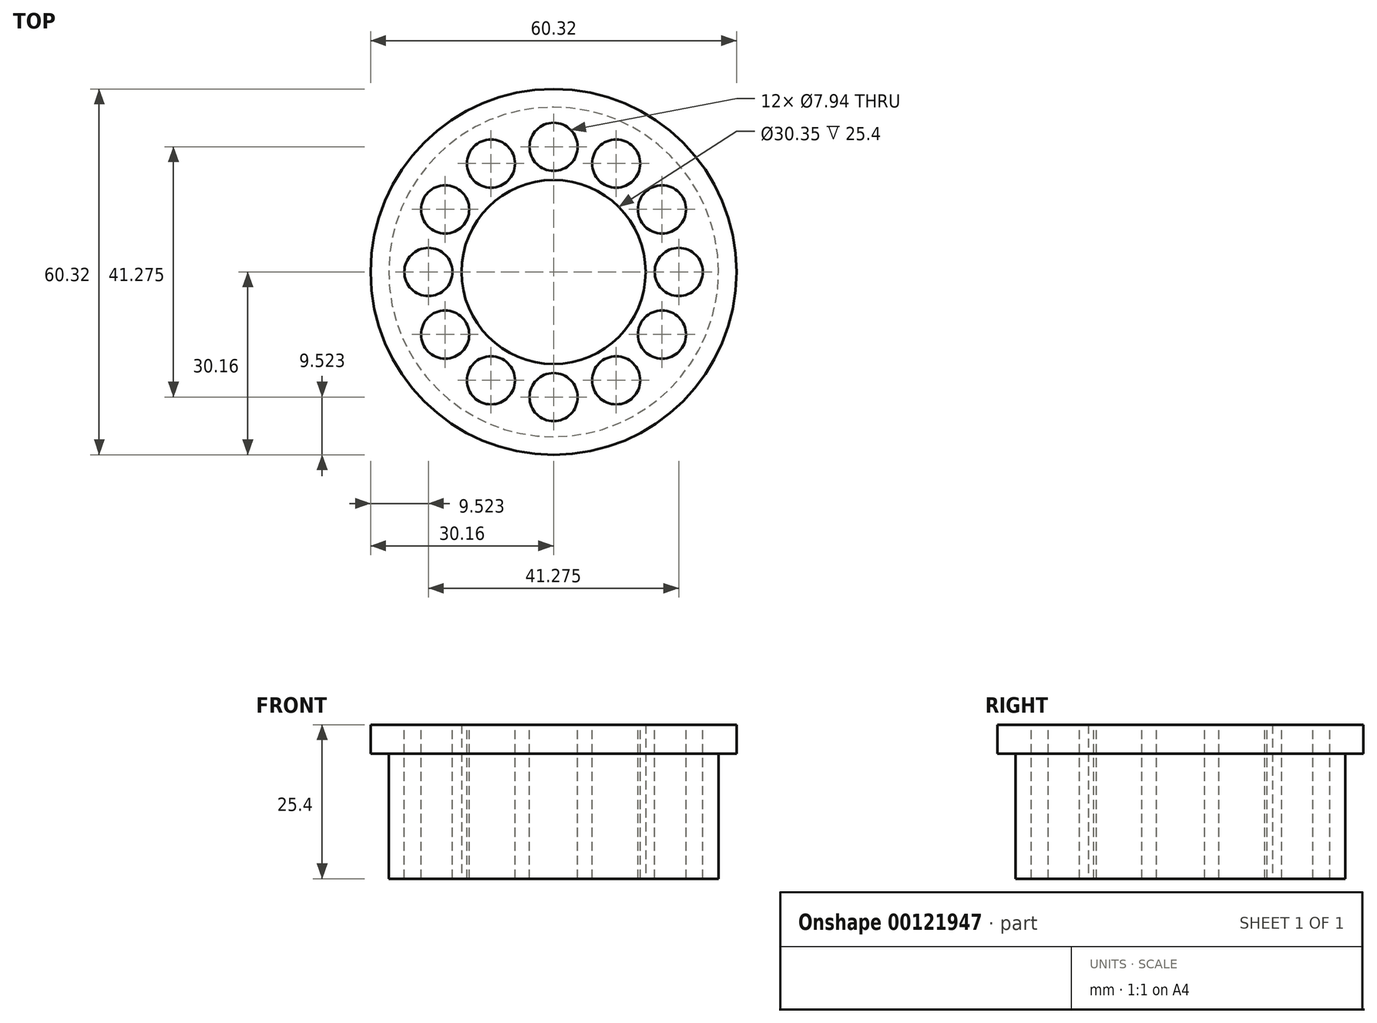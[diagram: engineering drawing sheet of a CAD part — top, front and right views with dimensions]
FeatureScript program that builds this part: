
annotation { "Feature Type Name" : "Feature", "Feature Type Description" : "" }
export const myFeature = defineFeature(function(context is Context, id is Id, definition is map)
    precondition{}
    {
        {
            var Q0;
            Q0=qCreatedBy(makeId("Front.planeOp"),FACE);
            var sketch = newSketch(context, id + "F0", { "sketchPlane" : qUnion([Q0])});
            skLineSegment(sketch, "E0", {"start": v(0, -9.36) * mm, "end": v(0, 13.63) * mm, "construction": true});
            skLineSegment(sketch, "E1", {"start": v(15.18, 0) * mm, "end": v(15.18, 25.4) * mm});
            skLineSegment(sketch, "E2", {"start": v(15.18, 25.4) * mm, "end": v(30.16, 25.4) * mm});
            skLineSegment(sketch, "E3", {"start": v(30.16, 25.4) * mm, "end": v(30.16, 20.64) * mm});
            skLineSegment(sketch, "E4", {"start": v(30.16, 20.64) * mm, "end": v(27.18, 20.64) * mm});
            skLineSegment(sketch, "E5", {"start": v(27.18, 20.64) * mm, "end": v(27.18, 0) * mm});
            skLineSegment(sketch, "E6", {"start": v(27.18, 0) * mm, "end": v(15.18, 0) * mm});
            skSolve(sketch);
        }
        {
            var Q0;
            Q0=makeQuery(id+"F0.imprint","IMPRINT",FACE,{"disambiguationData":[TD([[makeQuery(id+"F0.imprint","IMPRINT",EDGE,{"derivedFrom":sQuery(id+"F0.wireOp",EDGE,"E1")}),-1.0]])]});
            var Q1;
            Q1=sQuery(id+"F0.wireOp",EDGE,"E0");
            revolve(context, id + "F1", {"entities" : qUnion([Q0]), "axis" : qUnion([Q1]), "revolveType" : RevolveType.FULL});
        }
        {
            var Q0;
            Q0=makeQuery(id+"F1.opRevolve","SWEPT_FACE",FACE,{"disambiguationData":[OSD([sQuery(id+"F0.wireOp",EDGE,"E2")])]});
            var sketch = newSketch(context, id + "F2", { "sketchPlane" : qUnion([Q0])});
            skCircle(sketch, "E7", {"center": v(0, -20.64) * mm, "radius": 3.97 * mm});
            skCircle(sketch, "E8.1.0", {"center": v(10.32, -17.87) * mm, "radius": 3.97 * mm});
            skCircle(sketch, "E8.2.0", {"center": v(17.87, -10.32) * mm, "radius": 3.97 * mm});
            skCircle(sketch, "E8.3.0", {"center": v(20.64, 0) * mm, "radius": 3.97 * mm});
            skCircle(sketch, "E8.4.0", {"center": v(17.87, 10.32) * mm, "radius": 3.97 * mm});
            skCircle(sketch, "E8.5.0", {"center": v(10.32, 17.87) * mm, "radius": 3.97 * mm});
            skPoint(sketch, "E8.center", {"position": v(0, 0) * mm});
            skCircle(sketch, "E9.1.6.0", {"center": v(0, 20.64) * mm, "radius": 3.97 * mm});
            skCircle(sketch, "E9.1.7.0", {"center": v(-10.32, 17.87) * mm, "radius": 3.97 * mm});
            skCircle(sketch, "E10.1.8.0", {"center": v(-17.87, 10.32) * mm, "radius": 3.97 * mm});
            skCircle(sketch, "E10.1.9.0", {"center": v(-20.64, 0) * mm, "radius": 3.97 * mm});
            skCircle(sketch, "E10.1.10.0", {"center": v(-17.87, -10.32) * mm, "radius": 3.97 * mm});
            skCircle(sketch, "E10.1.11.0", {"center": v(-10.32, -17.87) * mm, "radius": 3.97 * mm});
            skSolve(sketch);
        }
        {
            var Q0;
            Q0=makeQuery(id+"F2.imprint","IMPRINT",FACE,{"disambiguationData":[TD([[makeQuery(id+"F2.imprint","IMPRINT",EDGE,{"derivedFrom":sQuery(id+"F2.wireOp",EDGE,"E7")}),1.0]])]});
            var Q1;
            Q1=makeQuery(id+"F2.imprint","IMPRINT",FACE,{"disambiguationData":[TD([[makeQuery(id+"F2.imprint","IMPRINT",EDGE,{"derivedFrom":sQuery(id+"F2.wireOp",EDGE,"E8.5.0")}),1.0]])]});
            var Q2;
            Q2=makeQuery(id+"F2.imprint","IMPRINT",FACE,{"disambiguationData":[TD([[makeQuery(id+"F2.imprint","IMPRINT",EDGE,{"derivedFrom":sQuery(id+"F2.wireOp",EDGE,"E8.4.0")}),1.0]])]});
            var Q3;
            Q3=makeQuery(id+"F2.imprint","IMPRINT",FACE,{"disambiguationData":[TD([[makeQuery(id+"F2.imprint","IMPRINT",EDGE,{"derivedFrom":sQuery(id+"F2.wireOp",EDGE,"E8.3.0")}),1.0]])]});
            var Q4;
            Q4=makeQuery(id+"F2.imprint","IMPRINT",FACE,{"disambiguationData":[TD([[makeQuery(id+"F2.imprint","IMPRINT",EDGE,{"derivedFrom":sQuery(id+"F2.wireOp",EDGE,"E8.2.0")}),1.0]])]});
            var Q5;
            Q5=makeQuery(id+"F2.imprint","IMPRINT",FACE,{"disambiguationData":[TD([[makeQuery(id+"F2.imprint","IMPRINT",EDGE,{"derivedFrom":sQuery(id+"F2.wireOp",EDGE,"E8.1.0")}),1.0]])]});
            var Q6;
            Q6=makeQuery(id+"F2.imprint","IMPRINT",FACE,{"disambiguationData":[TD([[makeQuery(id+"F2.imprint","IMPRINT",EDGE,{"derivedFrom":sQuery(id+"F2.wireOp",EDGE,"E10.1.11.0")}),1.0]])]});
            var Q7;
            Q7=makeQuery(id+"F2.imprint","IMPRINT",FACE,{"disambiguationData":[TD([[makeQuery(id+"F2.imprint","IMPRINT",EDGE,{"derivedFrom":sQuery(id+"F2.wireOp",EDGE,"E10.1.10.0")}),1.0]])]});
            var Q8;
            Q8=makeQuery(id+"F2.imprint","IMPRINT",FACE,{"disambiguationData":[TD([[makeQuery(id+"F2.imprint","IMPRINT",EDGE,{"derivedFrom":sQuery(id+"F2.wireOp",EDGE,"E10.1.9.0")}),1.0]])]});
            var Q9;
            Q9=makeQuery(id+"F2.imprint","IMPRINT",FACE,{"disambiguationData":[TD([[makeQuery(id+"F2.imprint","IMPRINT",EDGE,{"derivedFrom":sQuery(id+"F2.wireOp",EDGE,"E10.1.8.0")}),1.0]])]});
            var Q10;
            Q10=makeQuery(id+"F2.imprint","IMPRINT",FACE,{"disambiguationData":[TD([[makeQuery(id+"F2.imprint","IMPRINT",EDGE,{"derivedFrom":sQuery(id+"F2.wireOp",EDGE,"E9.1.7.0")}),1.0]])]});
            var Q11;
            Q11=makeQuery(id+"F2.imprint","IMPRINT",FACE,{"disambiguationData":[TD([[makeQuery(id+"F2.imprint","IMPRINT",EDGE,{"derivedFrom":sQuery(id+"F2.wireOp",EDGE,"E9.1.6.0")}),1.0]])]});
            extrude(context, id + "F3", {"entities" : qUnion([Q0, Q1, Q2, Q3, Q4, Q5, Q6, Q7, Q8, Q9, Q10, Q11]), "operationType" : NewBodyOperationType.REMOVE, "endBound" : BoundingType.THROUGH_ALL, "oppositeDirection" : true, "depth" : 25.4 * mm});
        }
    });
